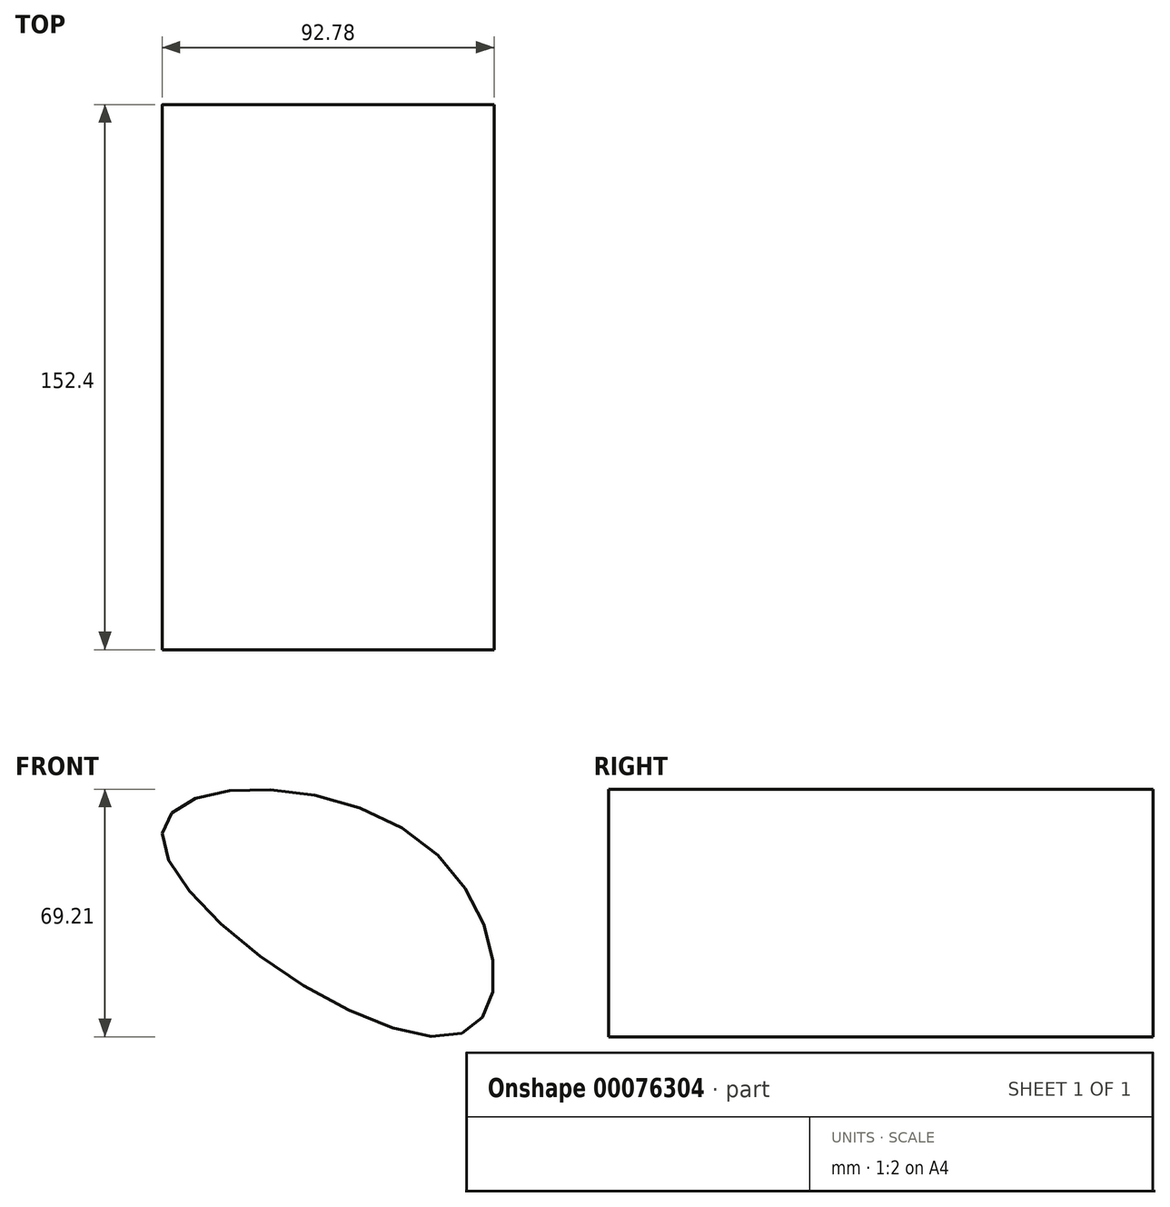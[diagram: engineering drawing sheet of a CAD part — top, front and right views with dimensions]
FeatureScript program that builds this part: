
annotation { "Feature Type Name" : "Feature", "Feature Type Description" : "" }
export const myFeature = defineFeature(function(context is Context, id is Id, definition is map)
    precondition{}
    {
        {
            var Q0;
            Q0=qCreatedBy(makeId("Front.planeOp"),FACE);
            var sketch = newSketch(context, id + "F0", { "sketchPlane" : qUnion([Q0])});
            skFitSpline(sketch, "E0", {"points": [v(-22.92, 32.3) * mm, v(50.34, 29.6) * mm, v(59.9, -23.82) * mm, v(-22.92, 32.3) * mm]});
            skSolve(sketch);
        }
        {
            var Q0;
            Q0=makeQuery(id+"F0.imprint","IMPRINT",FACE,{"disambiguationData":[TD([[makeQuery(id+"F0.imprint","IMPRINT",EDGE,{"derivedFrom":sQuery(id+"F0.wireOp",EDGE,"E0")}),-1.0]])]});
            extrude(context, id + "F1", {"entities" : qUnion([Q0]), "depth" : 127 * mm, "hasSecondDirection" : true, "secondDirectionOppositeDirection" : true, "secondDirectionDepth" : 25.4 * mm});
        }
    });
